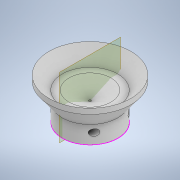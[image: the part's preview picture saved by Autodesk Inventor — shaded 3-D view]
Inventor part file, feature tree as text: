
AUTODESK INVENTOR PART (.ipt)
format: ipt  version: 2020 (Build 240168000, 168)  size: 178,688 bytes
history: native  units: in
note: dims shown in document units (in); Inventor stores cm internally (conversion verified against a paired STEP export)
features: sketch x4, hole x2, revolve x1, plane x1
ambient origin geometry x8: Origin, YZ Plane, XZ Plane, XY Plane, X Axis, Y Axis, Z Axis, Center Point
bodies: Solid1 (feature_tree)
feature tree (8):
  revolve  "Revolution1"  [1 undecoded]
  hole  "Hole1"  [1 undecoded]
  sketch  "Sketch3"  dims[d16=45.0deg d17=90.0deg]
  plane  "Work Plane1"
  hole  "Hole2"  [1 undecoded]
  sketch  "Sketch1"  dims[d7=90.0deg d8=0.211in]
  sketch  "Sketch2"  dims[d10=0.375in d11=0.25in d12=0.5635in d13=0.375in d14=0.0in d15=0.325in]
  sketch  "Sketch4"  dims[d18=0.4in d19=45.0deg d20=0.4in d21=135.0deg d22=0.177in d23=0.328in d24=0.332in d25=0.25in d26=0.5635in d27=0.484in d28=0.8108in d29=0.725in d30=0.389in d31=45.0deg d32=0.5in d33=45.0deg d34=0.146in d35=180.0deg d36=0.6in]
note: 3 required parameter values undecoded (feature->parameter linkage not recoverable at this tier; creation-order binding heuristic only, values carry confidence <= 0.55)